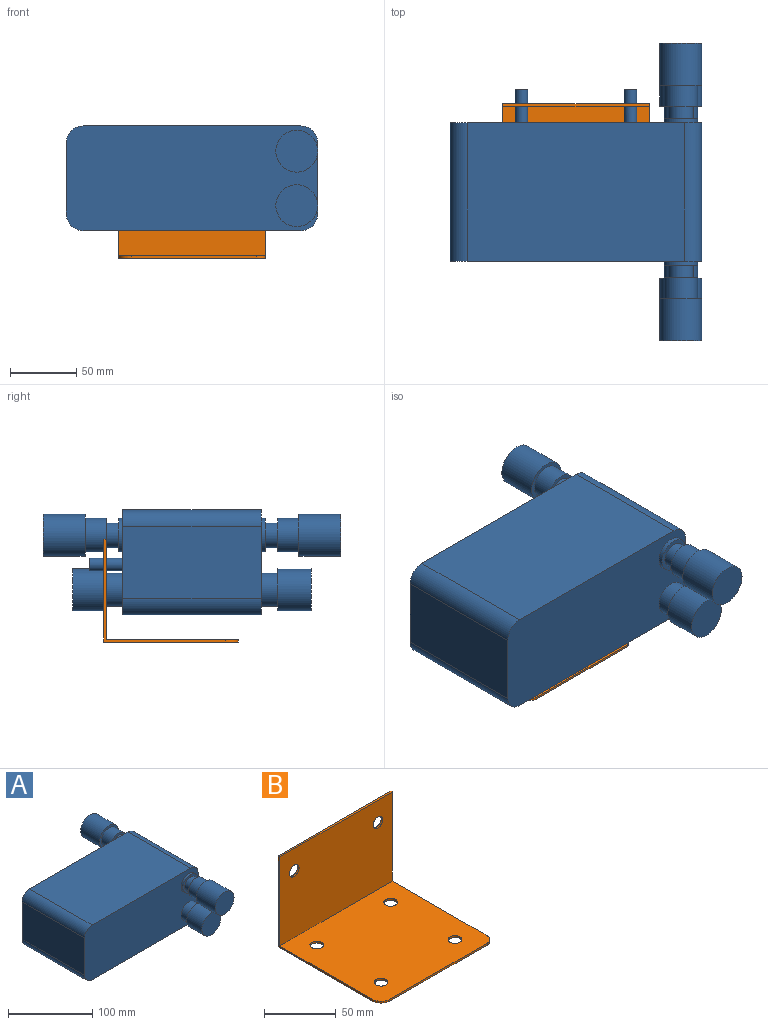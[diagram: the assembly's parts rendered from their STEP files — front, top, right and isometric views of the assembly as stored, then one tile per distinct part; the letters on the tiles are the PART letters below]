
ASSEMBLY  parts=2 mates=1
PART A: 38 faces, bbox 190.5x225.4x79.4 mm
  f0: plane 104.78x53.98mm, normal (1,0,0), area 5655.2mm2, adj f1,f7,f8,f9
  f1: cylinder r=12.7mm len=104.78mm, axis (0,1,0), area 2090.2mm2, adj f0,f2,f8,f9
  f2: plane 165.1x104.78mm, normal (0,0,1), area 17298.4mm2, adj f1,f3,f8,f9
  f3: cylinder r=12.7mm len=104.78mm, axis (0,1,0), area 2090.2mm2, adj f2,f4,f8,f9
  f4: plane 104.78x53.98mm, normal (-1,0,0), area 5655.2mm2, adj f3,f5,f8,f9
  f5: cylinder r=12.7mm len=104.78mm, axis (0,1,0), area 2090.2mm2, adj f4,f6,f8,f9
  f6: plane 165.1x104.78mm, normal (0,0,-1), area 17298.4mm2, adj f5,f7,f8,f9
  f7: cylinder r=12.7mm len=104.78mm, axis (0,1,0), area 2090.2mm2, adj f0,f6,f8,f9
  f8: plane 190.5x79.38mm, normal (0,-1,0), area 13969.1mm2, adj f0,f1,f2,f3,f4,f5,f6,f7
  f9: plane 190.5x79.38mm, normal (0,1,0), area 13826.6mm2, adj f0,f1,f2,f3,f4,f5,f6,f7
  f10: cylinder r=12.7mm len=25.4mm, axis (0,1,0), area 253.4mm2, adj f8,f11
  f11: plane 25.4x25.4mm, normal (0,-1,0), area 221.7mm2, adj f10,f12
  f12: cylinder r=9.53mm len=19.05mm, axis (0,1,0), area 570mm2, adj f11,f23
  f13: cylinder r=12.7mm len=25.4mm, axis (0,1,0), area 1013.4mm2, adj f8,f37
  f14: cylinder r=12.7mm len=25.4mm, axis (0,-1,0), area 253.4mm2, adj f9,f15
  f15: plane 25.4x25.4mm, normal (0,1,0), area 221.7mm2, adj f14,f16
  f16: cylinder r=9.53mm len=19.05mm, axis (0,-1,0), area 570mm2, adj f15,f28
  f17: cylinder r=12.7mm len=25.4mm, axis (0,-1,0), area 1013.4mm2, adj f9,f34
  f18: cylinder r=4.76mm len=25.4mm, axis (0,-1,0), area 760.1mm2, adj f9,f19
  f19: plane 9.53x9.53mm, normal (0,1,0), area 71.3mm2, adj f18
  f20: cylinder r=4.76mm len=25.4mm, axis (0,-1,0), area 760.1mm2, adj f9,f21
  f21: plane 9.53x9.53mm, normal (0,1,0), area 71.3mm2, adj f20
  f22: cylinder r=12.7mm len=25.4mm, axis (0,1,0), area 1266.8mm2, adj f23,f26
  f23: plane 25.4x25.4mm, normal (0,1,0), area 221.7mm2, adj f12,f22
  f24: cylinder r=15.88mm len=31.75mm, axis (0,1,0), area 3166.9mm2, adj f25,f26
  f25: plane 31.75x31.75mm, normal (0,-1,0), area 791.7mm2, adj f24
  f26: plane 31.75x31.75mm, normal (0,1,0), area 285mm2, adj f22,f24
  f27: cylinder r=12.7mm len=25.4mm, axis (0,-1,0), area 1266.8mm2, adj f28,f31
  f28: plane 25.4x25.4mm, normal (0,-1,0), area 221.7mm2, adj f16,f27
  f29: cylinder r=15.88mm len=31.75mm, axis (0,-1,0), area 3166.9mm2, adj f30,f31
  f30: plane 31.75x31.75mm, normal (0,1,0), area 791.7mm2, adj f29
  f31: plane 31.75x31.75mm, normal (0,-1,0), area 285mm2, adj f27,f29
  f32: cylinder r=15.88mm len=31.75mm, axis (0,-1,0), area 2533.5mm2, adj f33,f34
  f33: plane 31.75x31.75mm, normal (0,1,0), area 791.7mm2, adj f32
  f34: plane 31.75x31.75mm, normal (0,-1,0), area 285mm2, adj f17,f32
  f35: cylinder r=15.88mm len=31.75mm, axis (0,1,0), area 2533.5mm2, adj f36,f37
  f36: plane 31.75x31.75mm, normal (0,-1,0), area 791.7mm2, adj f35
  f37: plane 31.75x31.75mm, normal (0,1,0), area 285mm2, adj f13,f35
PART B: 16 faces, bbox 111.1x101.6x77.8 mm
  f0: plane 111.13x77.79mm, normal (0,1,0), area 8501.6mm2, adj f2,f9,f12,f13,f14,f15
  f1: plane 111.13x76.2mm, normal (0,-1,0), area 8325.2mm2, adj f2,f9,f11,f13,f14,f15
  f2: plane 92.08x77.79mm, normal (-1,0,0), area 267.1mm2, adj f0,f1,f3,f11,f12,f13
  f3: cylinder r=9.53mm len=9.53mm, axis (0,0,-1), area 23.8mm2, adj f2,f4,f11,f12
  f4: plane 95.25x1.59mm, normal (0,-1,0), area 151.2mm2, adj f3,f5,f11,f12
  f5: cylinder r=6.35mm len=6.35mm, axis (0,0,-1), area 15.8mm2, adj f4,f9,f11,f12
  f6: cylinder r=4.76mm len=9.53mm, axis (0,0,-1), area 47.5mm2, adj f11,f12
  f7: cylinder r=4.76mm len=9.53mm, axis (0,0,-1), area 47.5mm2, adj f11,f12
  f8: cylinder r=4.76mm len=9.53mm, axis (0,0,-1), area 47.5mm2, adj f11,f12
  f9: plane 95.25x77.79mm, normal (1,0,0), area 272.2mm2, adj f0,f1,f5,f11,f12,f13
  f10: cylinder r=4.76mm len=9.53mm, axis (0,0,-1), area 47.5mm2, adj f11,f12
  f11: plane 111.13x100.01mm, normal (0,0,1), area 10800.7mm2, adj f1,f2,f3,f4,f5,f6,f7,f8
  f12: plane 111.13x101.6mm, normal (0,0,-1), area 10977.2mm2, adj f0,f2,f3,f4,f5,f6,f7,f8
  f13: plane 111.13x1.59mm, normal (0,0,1), area 176.4mm2, adj f0,f1,f2,f9
  f14: cylinder r=4.76mm len=9.53mm, axis (0,-1,0), area 47.5mm2, adj f0,f1
  f15: cylinder r=4.76mm len=9.53mm, axis (0,-1,0), area 47.5mm2, adj f0,f1
PLACE A t=(-25.28,38.41,-12.56)mm
PLACE B t=(-25.28,1.9,-14.15)mm
MATE fastened A.f18 <-> B.f15  axis (0,1,0) through (16,63.81,44.59)mm
